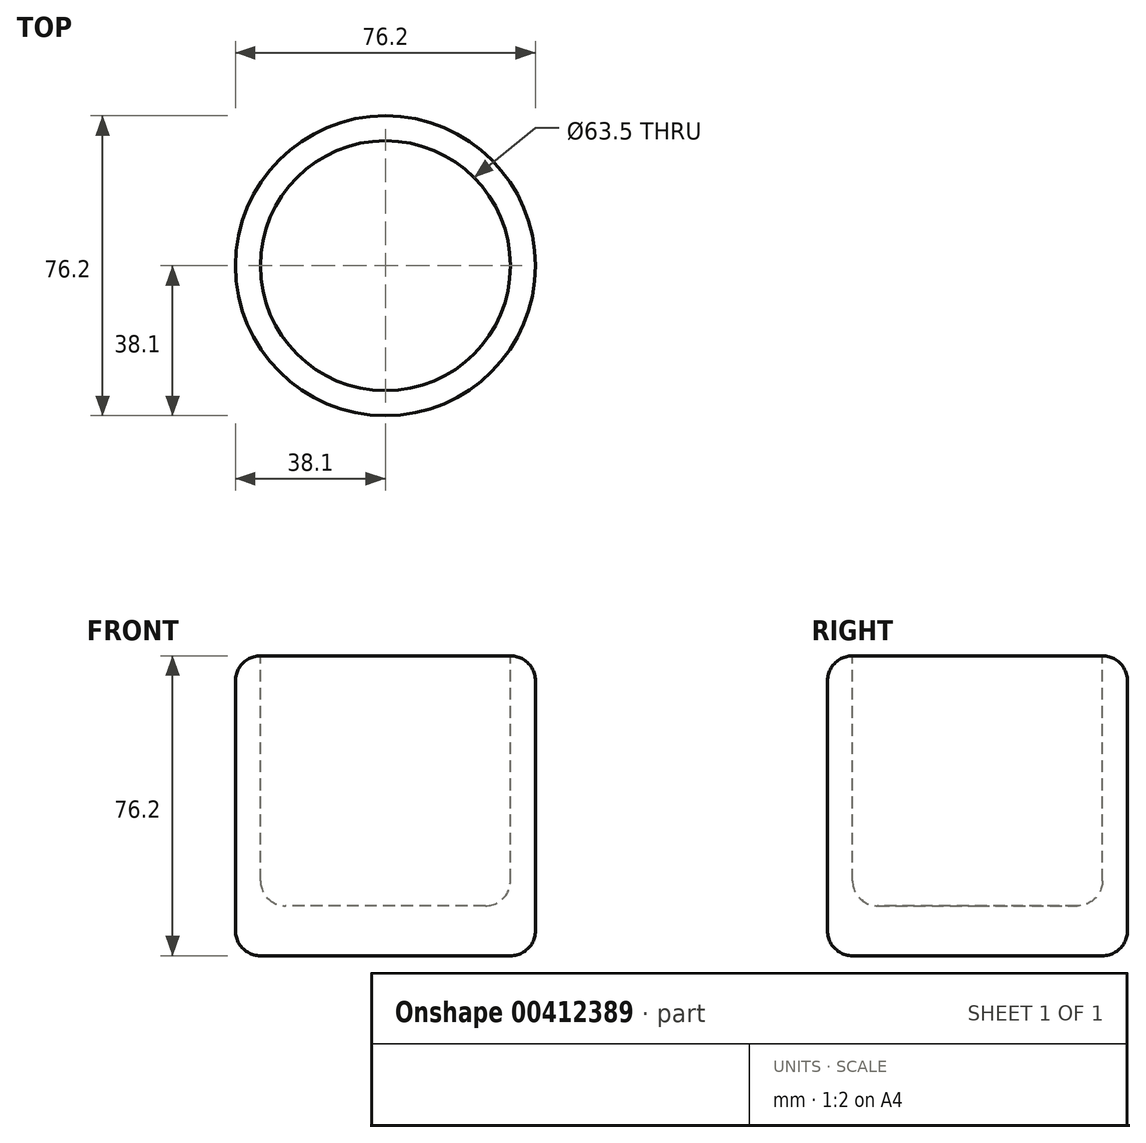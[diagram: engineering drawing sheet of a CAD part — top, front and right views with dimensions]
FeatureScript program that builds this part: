
annotation { "Feature Type Name" : "Feature", "Feature Type Description" : "" }
export const myFeature = defineFeature(function(context is Context, id is Id, definition is map)
    precondition{}
    {
        {
            var Q0;
            Q0=qCreatedBy(makeId("Top.planeOp"),FACE);
            var sketch = newSketch(context, id + "F0", { "sketchPlane" : qUnion([Q0])});
            skCircle(sketch, "E0", {"center": v(0, 0) * mm, "radius": 38.1 * mm});
            skSolve(sketch);
        }
        {
            var Q0;
            Q0 = qSketchRegion(id + "F0", true);
            extrude(context, id + "F1", {"entities" : qUnion([Q0]), "depth" : 76.2 * mm});
        }
        {
            var Q0;
            Q0=makeQuery(id+"F1.opExtrude","CAP_FACE",FACE,{"disambiguationData":[OSD([sQuery(id+"F0.wireOp",EDGE,"E0")])],"isStart":false});
            var Q1;
            Q1=makeQuery(id+"F1.opExtrude","CAP_EDGE",EDGE,{"disambiguationData":[OSD([sQuery(id+"F0.wireOp",EDGE,"E0")])],"isStart":true});
            fillet(context, id + "F2", {"entities" : qUnion([Q0, Q1]), "radius" : 6.35 * mm, "tangentPropagation" : true, "allowEdgeOverflow" : false});
        }
        {
            var Q0;
            Q0=makeQuery(id+"F1.opExtrude","CAP_FACE",FACE,{"disambiguationData":[OSD([sQuery(id+"F0.wireOp",EDGE,"E0")])],"isStart":false});
            var sketch = newSketch(context, id + "F3", { "sketchPlane" : qUnion([Q0])});
            skCircle(sketch, "E1.0", {"center": v(0, 0) * mm, "radius": 31.75 * mm});
            skSolve(sketch);
        }
        {
            var Q0;
            Q0 = qSketchRegion(id + "F3", true);
            extrude(context, id + "F4", {"entities" : qUnion([Q0]), "operationType" : NewBodyOperationType.REMOVE, "oppositeDirection" : true, "depth" : 63.5 * mm});
        }
        {
            var Q0;
            Q0=makeQuery(id+"F4.boolean.opBoolean","COPY",EDGE,{"derivedFrom":makeQuery(id+"F4.opExtrude","CAP_EDGE",EDGE,{"disambiguationData":[OSD([sQuery(id+"F3.wireOp",EDGE,"E1.0")])],"isStart":false})});
            fillet(context, id + "F5", {"entities" : qUnion([Q0]), "radius" : 6.35 * mm, "tangentPropagation" : true, "allowEdgeOverflow" : false});
        }
    });
